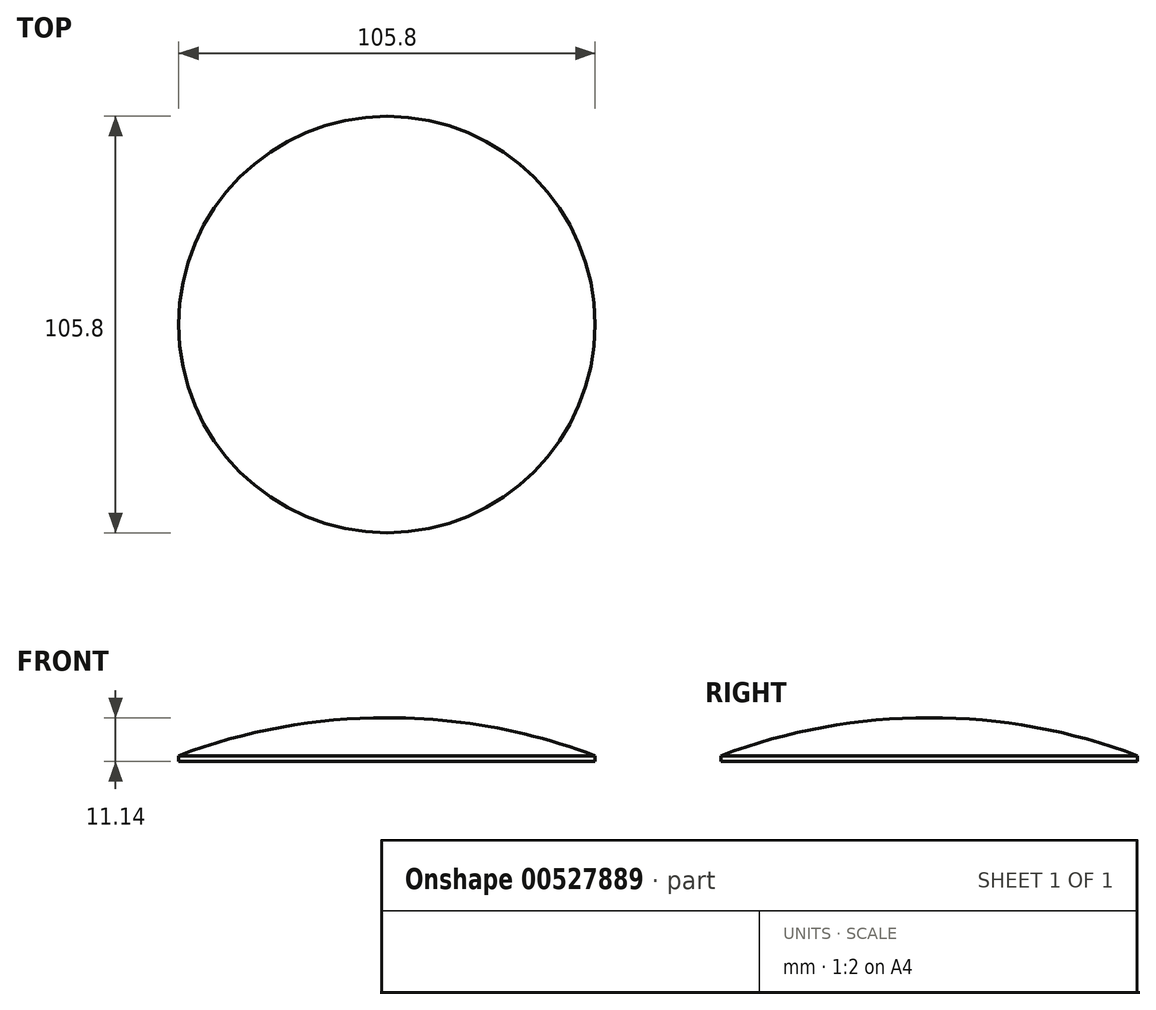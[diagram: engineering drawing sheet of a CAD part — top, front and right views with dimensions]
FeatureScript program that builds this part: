
annotation { "Feature Type Name" : "Feature", "Feature Type Description" : "" }
export const myFeature = defineFeature(function(context is Context, id is Id, definition is map)
    precondition{}
    {
        {
            var Q0;
            Q0=qCreatedBy(makeId("Front.planeOp"),FACE);
            var sketch = newSketch(context, id + "F0", { "sketchPlane" : qUnion([Q0])});
            skLineSegment(sketch, "E0", {"start": v(0, 0) * mm, "end": v(0, -150.02) * mm, "construction": true});
            skArc(sketch, "E1", {"start": v(52.9, -9.64) * mm, "mid": v(26.89, -2.43) * mm, "end": v(0, 0) * mm});
            skLineSegment(sketch, "E2", {"start": v(0, 0) * mm, "end": v(52.9, 0) * mm, "construction": true});
            skLineSegment(sketch, "E3", {"start": v(52.9, 0) * mm, "end": v(52.9, -9.64) * mm, "construction": true});
            skLineSegment(sketch, "E4", {"start": v(52.9, -9.64) * mm, "end": v(0, -9.64) * mm, "construction": true});
            skLineSegment(sketch, "E5", {"start": v(52.9, -9.64) * mm, "end": v(52.9, -11.14) * mm});
            skLineSegment(sketch, "E6", {"start": v(52.9, -11.14) * mm, "end": v(0, -11.14) * mm});
            skLineSegment(sketch, "E7", {"start": v(0, -11.14) * mm, "end": v(0, 0) * mm});
            skLineSegment(sketch, "E8.MirrorCS", {"start": v(0, -22.27) * mm, "end": v(0, 127.75) * mm, "construction": true});
            skLineSegment(sketch, "E9", {"start": v(111.82, -23.58) * mm, "end": v(136.82, -23.58) * mm});
            skLineSegment(sketch, "E10", {"start": v(111.82, -23.58) * mm, "end": v(111.82, 26.42) * mm});
            skLineSegment(sketch, "E11.MirrorCS", {"start": v(111.82, -23.58) * mm, "end": v(86.82, -23.58) * mm});
            skSolve(sketch);
        }
        {
            var Q0;
            Q0=qSketchRegion(id+"F0",true);
            var Q1;
            Q1=sQuery(id+"F0.wireOp",EDGE,"E7");
            revolve(context, id + "F1", {"entities" : qUnion([Q0]), "axis" : qUnion([Q1]), "revolveType" : RevolveType.FULL});
        }
    });
